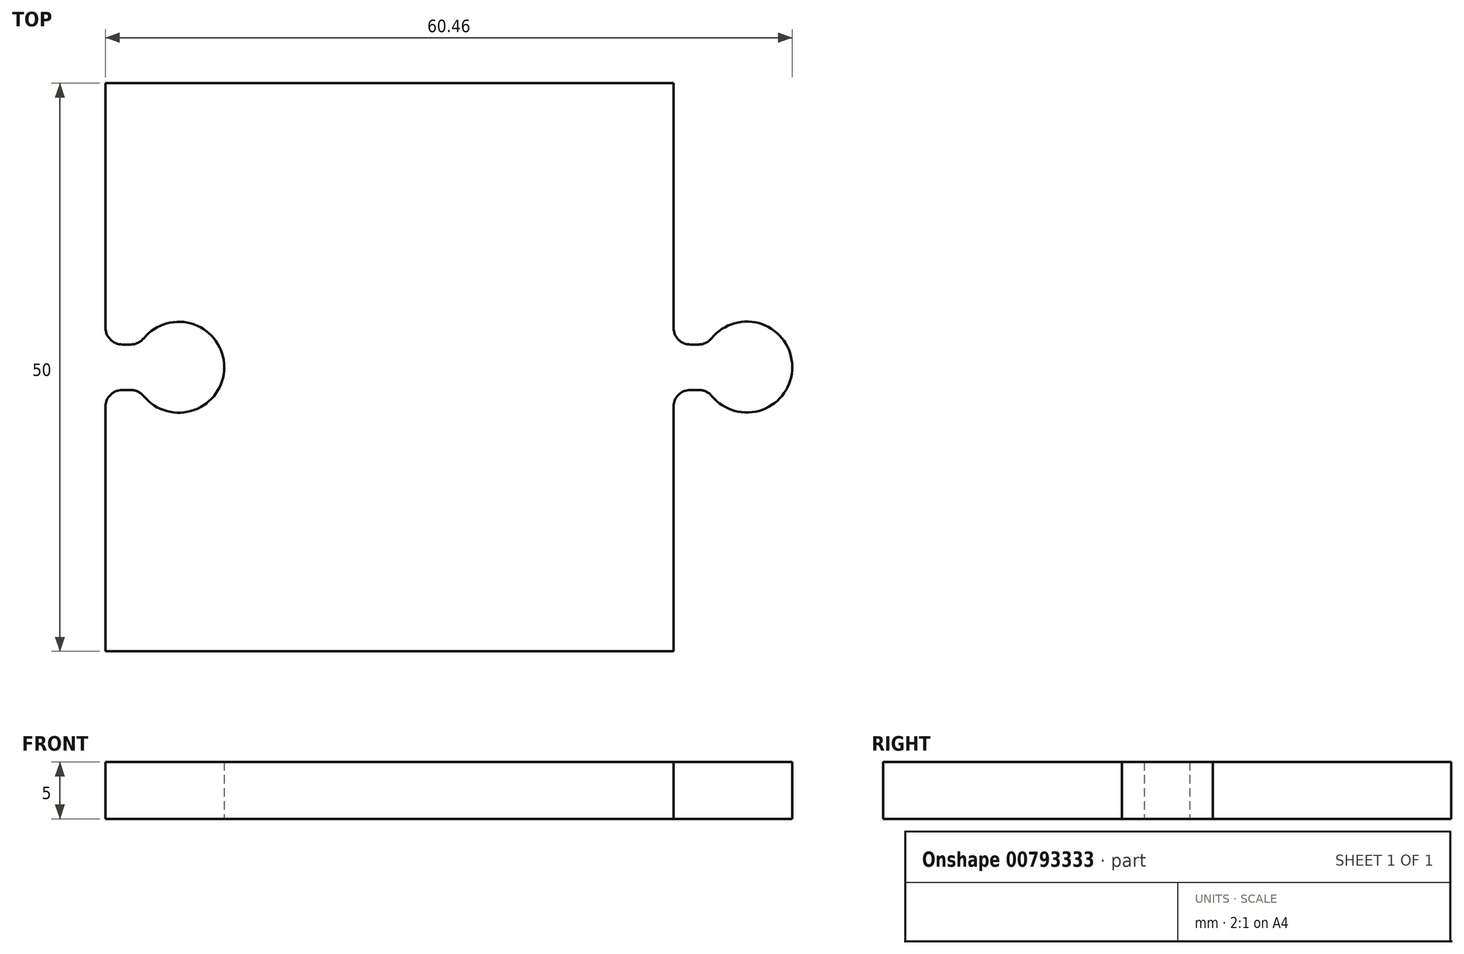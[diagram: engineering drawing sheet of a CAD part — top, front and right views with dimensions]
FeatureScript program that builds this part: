
annotation { "Feature Type Name" : "Feature", "Feature Type Description" : "" }
export const myFeature = defineFeature(function(context is Context, id is Id, definition is map)
    precondition{}
    {
        {
            var Q0;
            Q0=qCreatedBy(makeId("Top.planeOp"),FACE);
            var sketch = newSketch(context, id + "F0", { "sketchPlane" : qUnion([Q0])});
            skLineSegment(sketch, "E0.bottom", {"start": v(-29.6, 25) * mm, "end": v(20.4, 25) * mm});
            skLineSegment(sketch, "E0.top", {"start": v(-29.6, -25) * mm, "end": v(20.4, -25) * mm});
            skLineSegment(sketch, "E0.left", {"start": v(-29.6, 25) * mm, "end": v(-29.6, 3.5) * mm});
            skLineSegment(sketch, "E0.right", {"start": v(20.4, 25) * mm, "end": v(20.4, 3.5) * mm});
            skLineSegment(sketch, "E1", {"start": v(21.9, -2) * mm, "end": v(22.63, -2) * mm});
            skLineSegment(sketch, "E2", {"start": v(21.9, 2) * mm, "end": v(22.6, 2) * mm});
            skArc(sketch, "E3", {"start": v(23.78, -2.54) * mm, "mid": v(30.85, 0.03) * mm, "end": v(23.76, 2.55) * mm});
            skLineSegment(sketch, "E4.trimOffspring", {"start": v(30.33, 2) * mm, "end": v(30.33, 2) * mm});
            skLineSegment(sketch, "E5.trimOffspring", {"start": v(30.3, -2) * mm, "end": v(30.33, -2) * mm});
            skLineSegment(sketch, "E6", {"start": v(-28.1, -2) * mm, "end": v(-27.39, -2) * mm});
            skLineSegment(sketch, "E7", {"start": v(-28.1, 2) * mm, "end": v(-27.39, 2) * mm});
            skPoint(sketch, "E8.visualSharp", {"position": v(23.38, 2) * mm});
            skArc(sketch, "E8.filletArc", {"start": v(22.6, 2) * mm, "mid": v(23.24, 2.14) * mm, "end": v(23.76, 2.55) * mm});
            skPoint(sketch, "E9.visualSharp", {"position": v(23.4, -2) * mm});
            skArc(sketch, "E9.filletArc", {"start": v(23.78, -2.54) * mm, "mid": v(23.26, -2.14) * mm, "end": v(22.63, -2) * mm});
            skArc(sketch, "E10", {"start": v(-26.23, -2.55) * mm, "mid": v(-19.15, 0) * mm, "end": v(-26.23, 2.54) * mm});
            skPoint(sketch, "E11", {"position": v(20.4, 0.02) * mm});
            skLineSegment(sketch, "E12.trimOffspring", {"start": v(20.4, -3.5) * mm, "end": v(20.4, -25) * mm});
            skLineSegment(sketch, "E13.trimOffspring", {"start": v(-29.6, -3.5) * mm, "end": v(-29.6, -25) * mm});
            skPoint(sketch, "E14.visualSharp", {"position": v(-26.61, 2) * mm});
            skArc(sketch, "E14.filletArc", {"start": v(-27.39, 2) * mm, "mid": v(-26.75, 2.14) * mm, "end": v(-26.23, 2.54) * mm});
            skPoint(sketch, "E15.visualSharp", {"position": v(-26.61, -2) * mm});
            skArc(sketch, "E15.filletArc", {"start": v(-26.23, -2.55) * mm, "mid": v(-26.75, -2.14) * mm, "end": v(-27.39, -2) * mm});
            skPoint(sketch, "E16.visualSharp", {"position": v(20.4, 2) * mm});
            skArc(sketch, "E16.filletArc", {"start": v(20.4, 3.5) * mm, "mid": v(20.83, 2.44) * mm, "end": v(21.9, 2) * mm});
            skPoint(sketch, "E17.visualSharp", {"position": v(20.4, -2) * mm});
            skArc(sketch, "E17.filletArc", {"start": v(21.9, -2) * mm, "mid": v(20.83, -2.44) * mm, "end": v(20.4, -3.5) * mm});
            skPoint(sketch, "E18.visualSharp", {"position": v(-29.6, 2) * mm});
            skArc(sketch, "E18.filletArc", {"start": v(-29.6, 3.5) * mm, "mid": v(-29.17, 2.44) * mm, "end": v(-28.1, 2) * mm});
            skPoint(sketch, "E19.visualSharp", {"position": v(-29.6, -2) * mm});
            skArc(sketch, "E19.filletArc", {"start": v(-28.1, -2) * mm, "mid": v(-29.17, -2.44) * mm, "end": v(-29.6, -3.5) * mm});
            skSolve(sketch);
        }
        {
            var Q0;
            Q0 = qSketchRegion(id + "F0", true);
            extrude(context, id + "F1", {"entities" : qUnion([Q0]), "depth" : 5 * mm, "offsetDistance" : 25 * mm});
        }
    });
